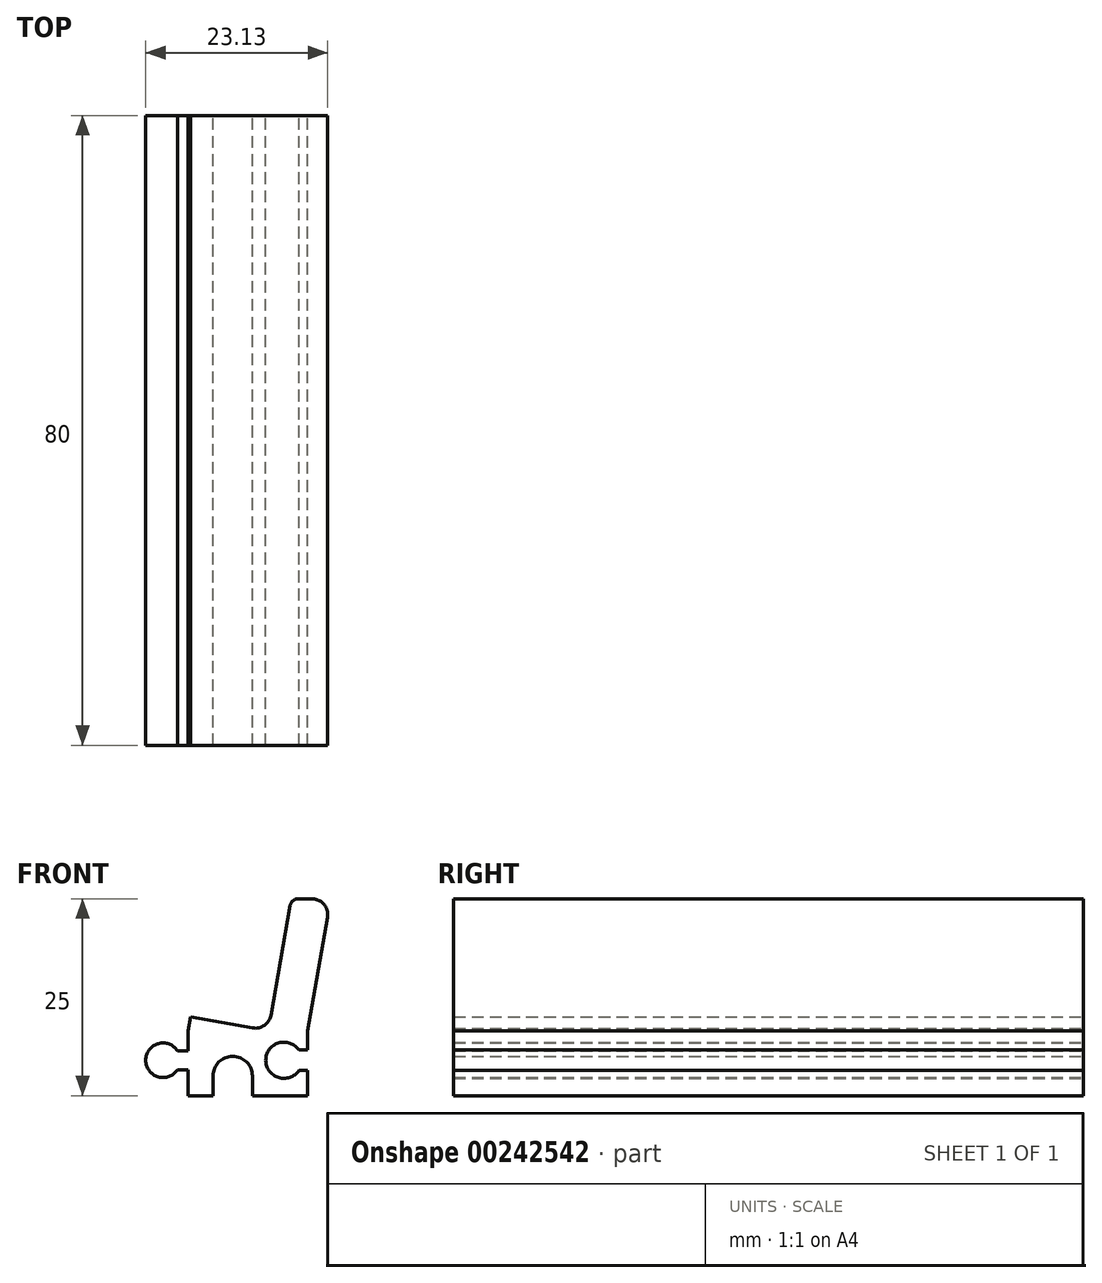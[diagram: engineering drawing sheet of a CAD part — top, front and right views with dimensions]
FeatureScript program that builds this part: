
annotation { "Feature Type Name" : "Feature", "Feature Type Description" : "" }
export const myFeature = defineFeature(function(context is Context, id is Id, definition is map)
    precondition{}
    {
        {
            var Q0;
            Q0=qCreatedBy(makeId("Front.planeOp"),FACE);
            var sketch = newSketch(context, id + "F0", { "sketchPlane" : qUnion([Q0])});
            skLineSegment(sketch, "E0", {"start": v(0, 0) * mm, "end": v(0, 25) * mm, "construction": true});
            skLineSegment(sketch, "E1", {"start": v(0, 25) * mm, "end": v(5, 25) * mm});
            skLineSegment(sketch, "E2", {"start": v(5, 25) * mm, "end": v(2.05, 8.26) * mm});
            skLineSegment(sketch, "E3", {"start": v(-2.95, 8.26) * mm, "end": v(0, 25) * mm});
            skArc(sketch, "E4", {"start": v(-4.95, 2.5) * mm, "mid": v(-7.45, 5) * mm, "end": v(-9.95, 2.5) * mm});
            skLineSegment(sketch, "E5", {"start": v(-4.95, 2.5) * mm, "end": v(-4.95, 0) * mm});
            skLineSegment(sketch, "E6", {"start": v(-9.95, 2.5) * mm, "end": v(-9.95, 0) * mm});
            skLineSegment(sketch, "E7", {"start": v(2.05, 8.26) * mm, "end": v(2.05, 5.8) * mm});
            skLineSegment(sketch, "E8", {"start": v(2.05, 0) * mm, "end": v(-4.95, 0) * mm});
            skArc(sketch, "E9", {"start": v(0.95, 5.8) * mm, "mid": v(-3.25, 4.5) * mm, "end": v(0.95, 3.2) * mm});
            skLineSegment(sketch, "E10", {"start": v(-0.95, 4.5) * mm, "end": v(2.05, 4.5) * mm, "construction": true});
            skLineSegment(sketch, "E11", {"start": v(0.95, 5.8) * mm, "end": v(2.05, 5.8) * mm});
            skLineSegment(sketch, "E12", {"start": v(0.95, 3.2) * mm, "end": v(2.05, 3.2) * mm});
            skLineSegment(sketch, "E13.trimOffspring", {"start": v(2.05, 3.2) * mm, "end": v(2.05, 0) * mm});
            skLineSegment(sketch, "E14", {"start": v(-2.95, 8.26) * mm, "end": v(-12.8, 10) * mm});
            skLineSegment(sketch, "E15", {"start": v(2.05, 8.26) * mm, "end": v(-25.76, 8.26) * mm, "construction": true});
            skLineSegment(sketch, "E16", {"start": v(-12.8, 10) * mm, "end": v(-13.1, 8.26) * mm});
            skLineSegment(sketch, "E17", {"start": v(-13.1, 8.26) * mm, "end": v(-13.1, 5.7) * mm});
            skLineSegment(sketch, "E18", {"start": v(-13.1, 0) * mm, "end": v(-9.95, 0) * mm});
            skLineSegment(sketch, "E19", {"start": v(-0.95, 4.5) * mm, "end": v(-28.63, 4.5) * mm, "construction": true});
            skArc(sketch, "E20", {"start": v(-14.46, 5.7) * mm, "mid": v(-18.5, 4.5) * mm, "end": v(-14.46, 3.3) * mm});
            skLineSegment(sketch, "E21", {"start": v(-14.46, 5.7) * mm, "end": v(-13.1, 5.7) * mm});
            skLineSegment(sketch, "E22", {"start": v(-14.46, 3.3) * mm, "end": v(-13.1, 3.3) * mm});
            skLineSegment(sketch, "E23.trimOffspring", {"start": v(-13.1, 3.3) * mm, "end": v(-13.1, 0) * mm});
            skSolve(sketch);
        }
        {
            var Q0;
            Q0 = qSketchRegion(id + "F0", true);
            extrude(context, id + "F1", {"entities" : qUnion([Q0]), "depth" : 80 * mm});
        }
        {
            var Q0;
            Q0=makeQuery(id+"F1.opExtrude","SWEPT_EDGE",EDGE,{"disambiguationData":[OSD([sQuery(id+"F0.wireOp",EDGE,"E1"),sQuery(id+"F0.wireOp",EDGE,"E2")])]});
            var Q1;
            Q1=makeQuery(id+"F1.opExtrude","SWEPT_EDGE",EDGE,{"disambiguationData":[OSD([sQuery(id+"F0.wireOp",EDGE,"E3"),sQuery(id+"F0.wireOp",EDGE,"E14")])]});
            fillet(context, id + "F2", {"entities" : qUnion([Q0, Q1]), "radius" : 2 * mm, "tangentPropagation" : true, "allowEdgeOverflow" : false});
        }
        {
            var Q0;
            Q0=makeQuery(id+"F1.opExtrude","SWEPT_EDGE",EDGE,{"disambiguationData":[OSD([sQuery(id+"F0.wireOp",EDGE,"E1"),sQuery(id+"F0.wireOp",EDGE,"E3")])]});
            fillet(context, id + "F3", {"entities" : qUnion([Q0]), "radius" : 1 * mm, "tangentPropagation" : true, "allowEdgeOverflow" : false});
        }
    });
